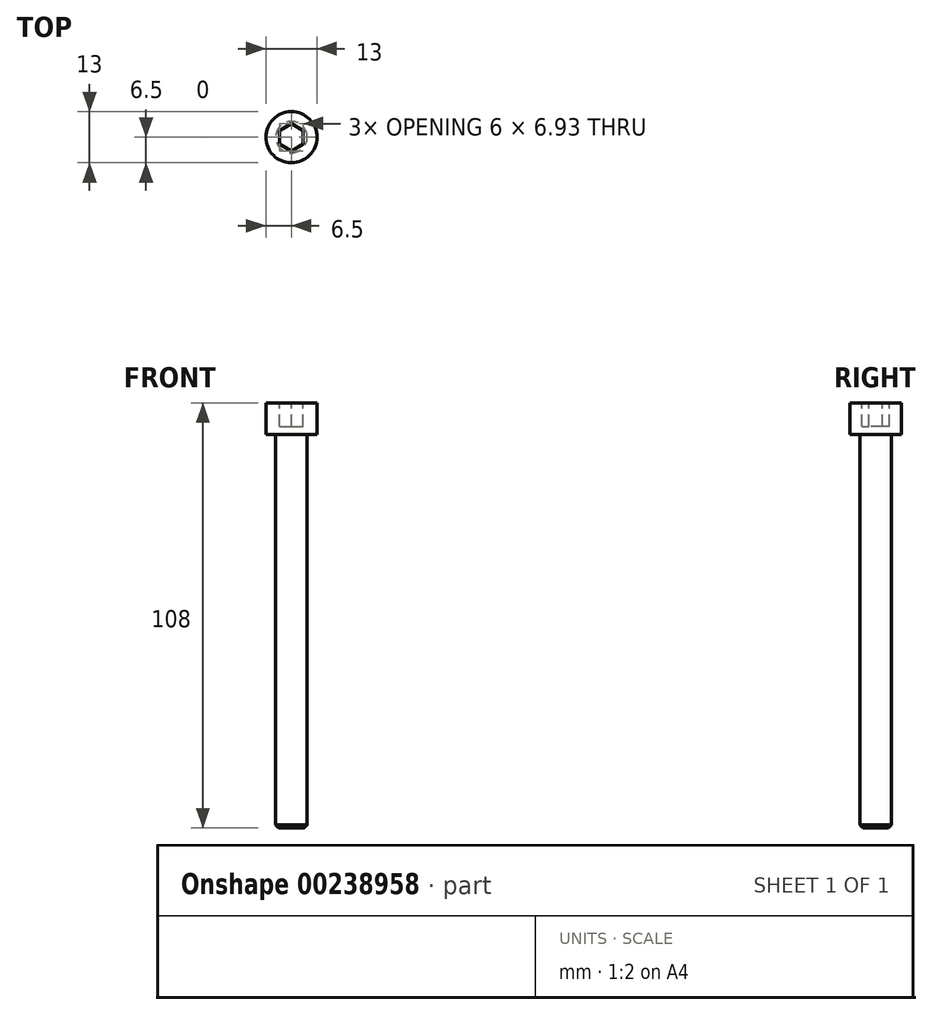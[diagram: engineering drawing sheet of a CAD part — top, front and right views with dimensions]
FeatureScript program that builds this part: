
annotation { "Feature Type Name" : "Feature", "Feature Type Description" : "" }
export const myFeature = defineFeature(function(context is Context, id is Id, definition is map)
    precondition{}
    {
        {
            var Q0;
            Q0=qCreatedBy(makeId("Front.planeOp"),FACE);
            var sketch = newSketch(context, id + "F0", { "sketchPlane" : qUnion([Q0])});
            skLineSegment(sketch, "E0", {"start": v(-6.5, 8) * mm, "end": v(-6.5, 0) * mm});
            skLineSegment(sketch, "E1", {"start": v(-6.5, 8) * mm, "end": v(0, 8) * mm});
            skLineSegment(sketch, "E2", {"start": v(-4, 0) * mm, "end": v(-4, -99.23) * mm});
            skCircle(sketch, "E3", {"center": v(0, 0) * mm, "radius": 3.24 * mm, "construction": true});
            skLineSegment(sketch, "E4", {"start": v(0, -100) * mm, "end": v(-3.23, -100) * mm});
            skLineSegment(sketch, "E5", {"start": v(-3.23, 0) * mm, "end": v(-3.23, -42.56) * mm, "construction": true});
            skLineSegment(sketch, "E6", {"start": v(-3.24, -100) * mm, "end": v(-4, -99.23) * mm});
            skLineSegment(sketch, "E7", {"start": v(-6.5, 0) * mm, "end": v(-4, 0) * mm});
            skLineSegment(sketch, "E8", {"start": v(0, 8) * mm, "end": v(0, -100) * mm});
            skSolve(sketch);
        }
        {
            var Q0;
            Q0 = qSketchRegion(id + "F0", true);
            var Q1;
            Q1=sQuery(id+"F0.wireOp",EDGE,"E8");
            revolve(context, id + "F1", {"entities" : qUnion([Q0]), "axis" : qUnion([Q1]), "revolveType" : RevolveType.FULL});
        }
        {
            var Q0;
            Q0=makeQuery(id+"F1.opRevolve","SWEPT_FACE",FACE,{"disambiguationData":[OSD([sQuery(id+"F0.wireOp",EDGE,"E1")])]});
            cPlane(context, id + "F2", {"entities" : qUnion([Q0]), "cplaneType" : CPlaneType.OFFSET, "offset" : 0 * mm, "width" : 150 * mm, "height" : 150 * mm});
        }
        {
            var Q0;
            Q0=qCreatedBy(id+"F2.planeOp",FACE);
            var sketch = newSketch(context, id + "F3", { "sketchPlane" : qUnion([Q0])});
            skCircle(sketch, "E9.cCircle", {"center": v(0, 0) * mm, "radius": 3 * mm, "construction": true});
            skLineSegment(sketch, "E9.0", {"start": v(3, 1.73) * mm, "end": v(3, -1.73) * mm});
            skLineSegment(sketch, "E9.1", {"start": v(3, -1.73) * mm, "end": v(0, -3.46) * mm});
            skLineSegment(sketch, "E9.2", {"start": v(0, -3.46) * mm, "end": v(-3, -1.73) * mm});
            skLineSegment(sketch, "E9.3", {"start": v(-3, -1.73) * mm, "end": v(-3, 1.73) * mm});
            skLineSegment(sketch, "E9.4", {"start": v(-3, 1.73) * mm, "end": v(0, 3.46) * mm});
            skLineSegment(sketch, "E9.5", {"start": v(0, 3.46) * mm, "end": v(3, 1.73) * mm});
            skPoint(sketch, "E9.0.midPoint", {"position": v(3, 0) * mm});
            skSolve(sketch);
        }
        {
            var Q0;
            Q0 = qSketchRegion(id + "F3", true);
            extrude(context, id + "F4", {"entities" : qUnion([Q0]), "operationType" : NewBodyOperationType.REMOVE, "oppositeDirection" : true, "depth" : 6 * mm, "hasSecondDirection" : true, "secondDirectionOppositeDirection" : false, "secondDirectionDepth" : 6 * mm});
        }
    });
